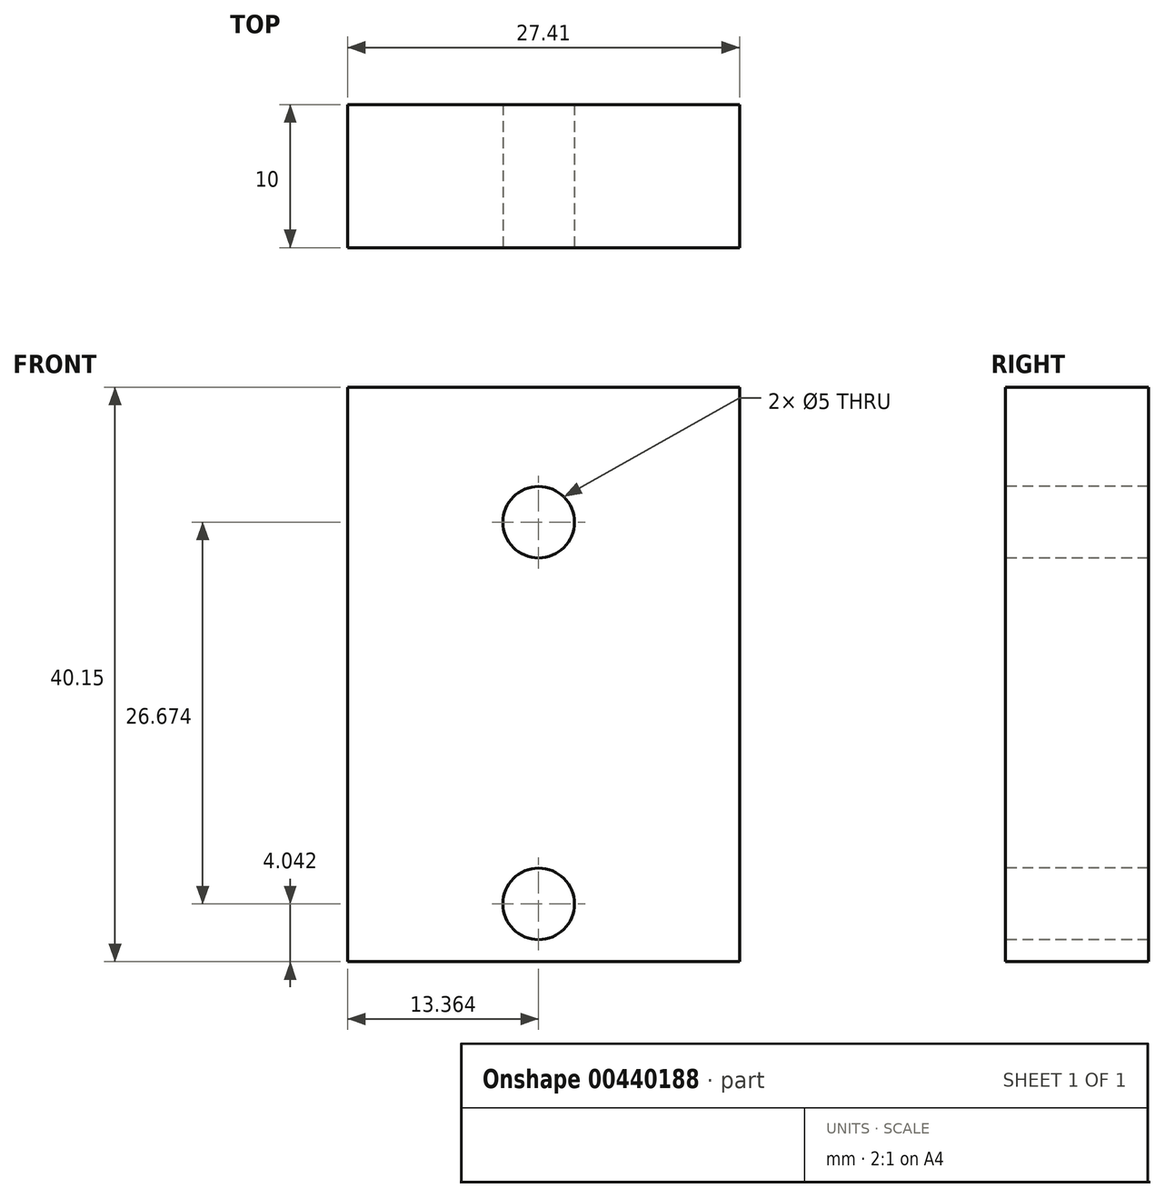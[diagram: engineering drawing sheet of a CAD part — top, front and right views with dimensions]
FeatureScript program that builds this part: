
annotation { "Feature Type Name" : "Feature", "Feature Type Description" : "" }
export const myFeature = defineFeature(function(context is Context, id is Id, definition is map)
    precondition{}
    {
        {
            var Q0;
            Q0=qCreatedBy(makeId("Front.planeOp"),FACE);
            var sketch = newSketch(context, id + "F0", { "sketchPlane" : qUnion([Q0])});
            skLineSegment(sketch, "E0.bottom", {"start": v(0, 0) * mm, "end": v(27.41, 0) * mm});
            skLineSegment(sketch, "E0.top", {"start": v(0, 40.15) * mm, "end": v(27.41, 40.15) * mm});
            skLineSegment(sketch, "E0.left", {"start": v(0, 0) * mm, "end": v(0, 40.15) * mm});
            skLineSegment(sketch, "E0.right", {"start": v(27.41, 0) * mm, "end": v(27.41, 40.15) * mm});
            skSolve(sketch);
        }
        {
            var Q0;
            Q0=makeQuery(id+"F0.imprint","IMPRINT",FACE,{"disambiguationData":[TD([[makeQuery(id+"F0.imprint","IMPRINT",EDGE,{"derivedFrom":sQuery(id+"F0.wireOp",EDGE,"E0.bottom")}),1.0]])]});
            extrude(context, id + "F1", {"entities" : qUnion([Q0]), "depth" : 10 * mm});
        }
        {
            var Q0;
            Q0=makeQuery(id+"F1.opExtrude","CAP_FACE",FACE,{"disambiguationData":[OSD([sQuery(id+"F0.wireOp",EDGE,"E0.bottom"),sQuery(id+"F0.wireOp",EDGE,"E0.top"),sQuery(id+"F0.wireOp",EDGE,"E0.left"),sQuery(id+"F0.wireOp",EDGE,"E0.right")])],"isStart":false});
            var sketch = newSketch(context, id + "F2", { "sketchPlane" : qUnion([Q0])});
            skCircle(sketch, "E1", {"center": v(13.36, 30.72) * mm, "radius": 1.69 * mm});
            skCircle(sketch, "E2", {"center": v(13.36, 4.04) * mm, "radius": 2.22 * mm});
            skSolve(sketch);
        }
        {
            var Q0;
            Q0=sQuery(id+"F2.wireOp",VERTEX,"E2.center");
            var Q1;
            Q1=sQuery(id+"F2.wireOp",VERTEX,"E1.center");
            var Q2;
            Q2=makeQuery(id+"F1.opExtrude","SWEPT_BODY",BODY,{"disambiguationData":[OSD([sQuery(id+"F0.wireOp",EDGE,"E0.bottom"),sQuery(id+"F0.wireOp",EDGE,"E0.top"),sQuery(id+"F0.wireOp",EDGE,"E0.left"),sQuery(id+"F0.wireOp",EDGE,"E0.right")])]});
            hole(context, id + "F3", {"style" : HoleStyle.SIMPLE, "endStyle" : HoleEndStyle.THROUGH, "holeDiameter" : 5 * mm, "isTappedThrough" : true, "tappedDepth" : 12 * mm, "tapClearance" : 3, "locations" : qUnion([Q0, Q1]), "scope" : qUnion([Q2])});
        }
    });
